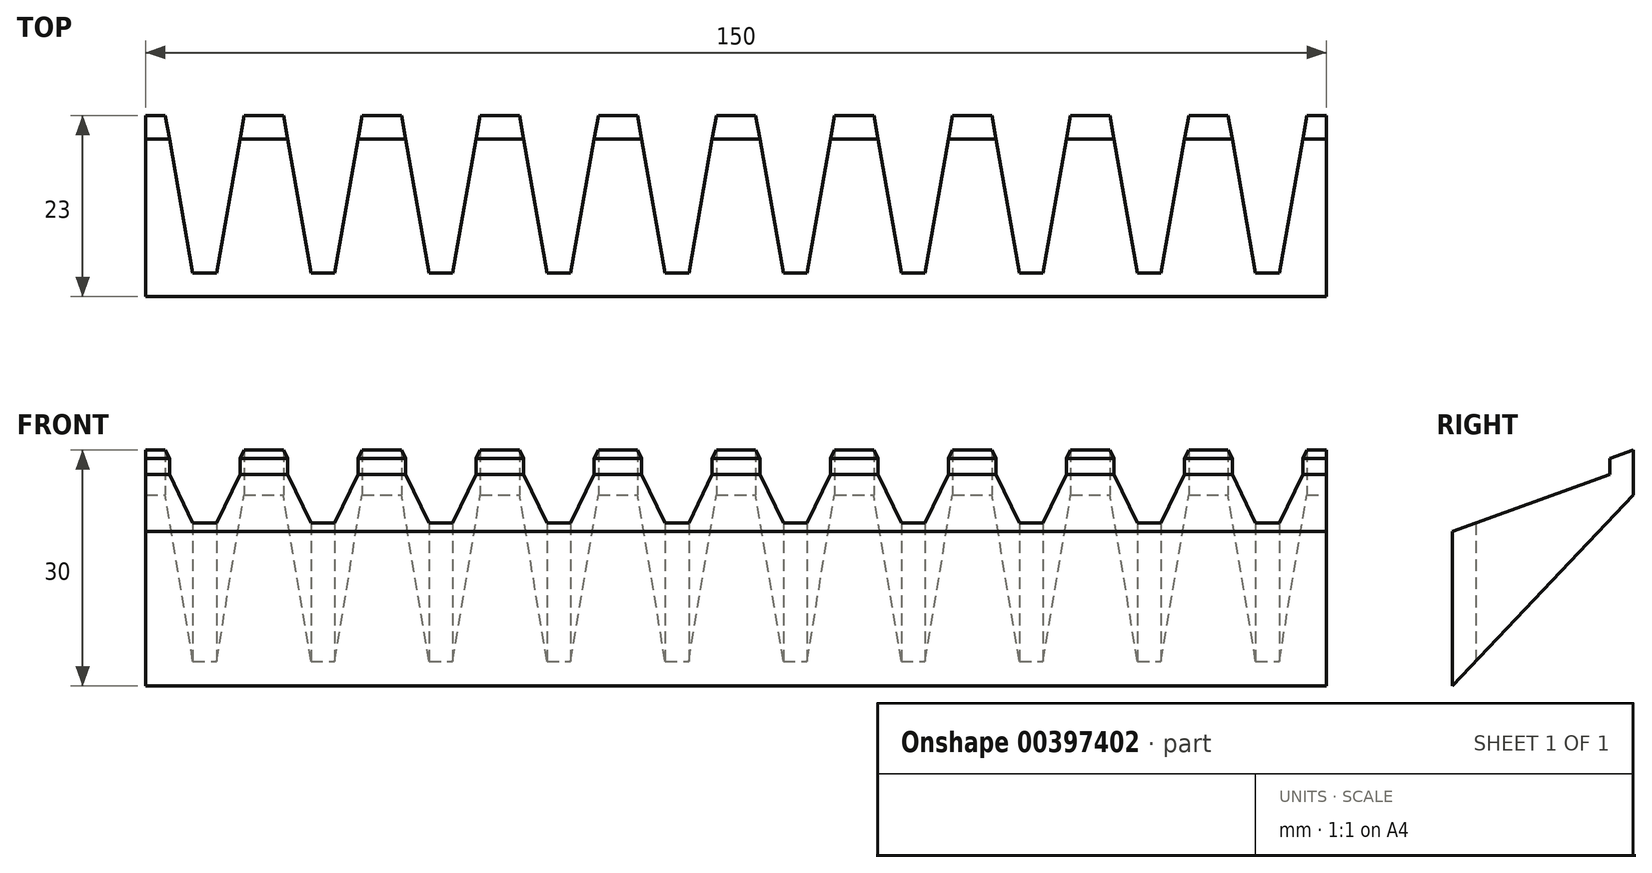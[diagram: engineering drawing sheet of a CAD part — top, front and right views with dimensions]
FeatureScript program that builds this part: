
annotation { "Feature Type Name" : "Feature", "Feature Type Description" : "" }
export const myFeature = defineFeature(function(context is Context, id is Id, definition is map)
    precondition{}
    {
        {
            var Q0;
            Q0=qCreatedBy(makeId("Top.planeOp"),FACE);
            var sketch = newSketch(context, id + "F0", { "sketchPlane" : qUnion([Q0])});
            skLineSegment(sketch, "E0", {"start": v(0, 0) * mm, "end": v(0, 52.8) * mm, "construction": true});
            skLineSegment(sketch, "E1", {"start": v(-7.5, 23) * mm, "end": v(-5, 23) * mm});
            skLineSegment(sketch, "E2", {"start": v(-5, 23) * mm, "end": v(-1.5, 3) * mm});
            skLineSegment(sketch, "E3", {"start": v(-1.5, 3) * mm, "end": v(0, 3) * mm});
            skLineSegment(sketch, "E4", {"start": v(-7.5, 23) * mm, "end": v(-7.5, 0) * mm});
            skLineSegment(sketch, "E5.MirrorCS", {"start": v(7.5, 23) * mm, "end": v(7.5, 0) * mm, "construction": true});
            skLineSegment(sketch, "E6.MirrorCS", {"start": v(5, 23) * mm, "end": v(1.5, 3) * mm});
            skLineSegment(sketch, "E7.MirrorCS", {"start": v(1.5, 3) * mm, "end": v(0, 3) * mm});
            skLineSegment(sketch, "E8.MirrorCS", {"start": v(7.5, 23) * mm, "end": v(5, 23) * mm});
            skLineSegment(sketch, "E9.1.0.0", {"start": v(20, 23) * mm, "end": v(16.5, 3) * mm});
            skLineSegment(sketch, "E9.1.0.1", {"start": v(22.5, 23) * mm, "end": v(20, 23) * mm});
            skLineSegment(sketch, "E9.1.0.2", {"start": v(22.5, 23) * mm, "end": v(22.5, 0) * mm, "construction": true});
            skLineSegment(sketch, "E9.1.0.4", {"start": v(10, 23) * mm, "end": v(13.5, 3) * mm});
            skLineSegment(sketch, "E9.1.0.5", {"start": v(7.5, 23) * mm, "end": v(10, 23) * mm});
            skLineSegment(sketch, "E9.1.0.6", {"start": v(16.5, 3) * mm, "end": v(15, 3) * mm});
            skLineSegment(sketch, "E9.1.0.7", {"start": v(13.5, 3) * mm, "end": v(15, 3) * mm});
            skLineSegment(sketch, "E9.2.0.0", {"start": v(35, 23) * mm, "end": v(31.5, 3) * mm});
            skLineSegment(sketch, "E9.2.0.1", {"start": v(37.5, 23) * mm, "end": v(35, 23) * mm});
            skLineSegment(sketch, "E9.2.0.2", {"start": v(37.5, 23) * mm, "end": v(37.5, 0) * mm, "construction": true});
            skLineSegment(sketch, "E9.2.0.3", {"start": v(22.5, 23) * mm, "end": v(22.5, 0) * mm, "construction": true});
            skLineSegment(sketch, "E9.2.0.4", {"start": v(25, 23) * mm, "end": v(28.5, 3) * mm});
            skLineSegment(sketch, "E9.2.0.5", {"start": v(22.5, 23) * mm, "end": v(25, 23) * mm});
            skLineSegment(sketch, "E9.2.0.6", {"start": v(31.5, 3) * mm, "end": v(30, 3) * mm});
            skLineSegment(sketch, "E9.2.0.7", {"start": v(28.5, 3) * mm, "end": v(30, 3) * mm});
            skLineSegment(sketch, "E9.3.0.0", {"start": v(50, 23) * mm, "end": v(46.5, 3) * mm});
            skLineSegment(sketch, "E9.3.0.1", {"start": v(52.5, 23) * mm, "end": v(50, 23) * mm});
            skLineSegment(sketch, "E9.3.0.2", {"start": v(52.5, 23) * mm, "end": v(52.5, 0) * mm, "construction": true});
            skLineSegment(sketch, "E9.3.0.3", {"start": v(37.5, 23) * mm, "end": v(37.5, 0) * mm, "construction": true});
            skLineSegment(sketch, "E9.3.0.4", {"start": v(40, 23) * mm, "end": v(43.5, 3) * mm});
            skLineSegment(sketch, "E9.3.0.5", {"start": v(37.5, 23) * mm, "end": v(40, 23) * mm});
            skLineSegment(sketch, "E9.3.0.6", {"start": v(46.5, 3) * mm, "end": v(45, 3) * mm});
            skLineSegment(sketch, "E9.3.0.7", {"start": v(43.5, 3) * mm, "end": v(45, 3) * mm});
            skLineSegment(sketch, "E9.4.0.0", {"start": v(65, 23) * mm, "end": v(61.5, 3) * mm});
            skLineSegment(sketch, "E9.4.0.1", {"start": v(67.5, 23) * mm, "end": v(65, 23) * mm});
            skLineSegment(sketch, "E9.4.0.2", {"start": v(67.5, 23) * mm, "end": v(67.5, 0) * mm, "construction": true});
            skLineSegment(sketch, "E9.4.0.3", {"start": v(52.5, 23) * mm, "end": v(52.5, 0) * mm, "construction": true});
            skLineSegment(sketch, "E9.4.0.4", {"start": v(55, 23) * mm, "end": v(58.5, 3) * mm});
            skLineSegment(sketch, "E9.4.0.5", {"start": v(52.5, 23) * mm, "end": v(55, 23) * mm});
            skLineSegment(sketch, "E9.4.0.6", {"start": v(61.5, 3) * mm, "end": v(60, 3) * mm});
            skLineSegment(sketch, "E9.4.0.7", {"start": v(58.5, 3) * mm, "end": v(60, 3) * mm});
            skLineSegment(sketch, "E9.5.0.0", {"start": v(80, 23) * mm, "end": v(76.5, 3) * mm});
            skLineSegment(sketch, "E9.5.0.1", {"start": v(82.5, 23) * mm, "end": v(80, 23) * mm});
            skLineSegment(sketch, "E9.5.0.2", {"start": v(82.5, 23) * mm, "end": v(82.5, 0) * mm, "construction": true});
            skLineSegment(sketch, "E9.5.0.3", {"start": v(67.5, 23) * mm, "end": v(67.5, 0) * mm, "construction": true});
            skLineSegment(sketch, "E9.5.0.4", {"start": v(70, 23) * mm, "end": v(73.5, 3) * mm});
            skLineSegment(sketch, "E9.5.0.5", {"start": v(67.5, 23) * mm, "end": v(70, 23) * mm});
            skLineSegment(sketch, "E9.5.0.6", {"start": v(76.5, 3) * mm, "end": v(75, 3) * mm});
            skLineSegment(sketch, "E9.5.0.7", {"start": v(73.5, 3) * mm, "end": v(75, 3) * mm});
            skLineSegment(sketch, "E9.6.0.0", {"start": v(95, 23) * mm, "end": v(91.5, 3) * mm});
            skLineSegment(sketch, "E9.6.0.1", {"start": v(97.5, 23) * mm, "end": v(95, 23) * mm});
            skLineSegment(sketch, "E9.6.0.2", {"start": v(97.5, 23) * mm, "end": v(97.5, 0) * mm, "construction": true});
            skLineSegment(sketch, "E9.6.0.3", {"start": v(82.5, 23) * mm, "end": v(82.5, 0) * mm, "construction": true});
            skLineSegment(sketch, "E9.6.0.4", {"start": v(85, 23) * mm, "end": v(88.5, 3) * mm});
            skLineSegment(sketch, "E9.6.0.5", {"start": v(82.5, 23) * mm, "end": v(85, 23) * mm});
            skLineSegment(sketch, "E9.6.0.6", {"start": v(91.5, 3) * mm, "end": v(90, 3) * mm});
            skLineSegment(sketch, "E9.6.0.7", {"start": v(88.5, 3) * mm, "end": v(90, 3) * mm});
            skLineSegment(sketch, "E9.7.0.0", {"start": v(110, 23) * mm, "end": v(106.5, 3) * mm});
            skLineSegment(sketch, "E9.7.0.1", {"start": v(112.5, 23) * mm, "end": v(110, 23) * mm});
            skLineSegment(sketch, "E9.7.0.2", {"start": v(112.5, 23) * mm, "end": v(112.5, 0) * mm, "construction": true});
            skLineSegment(sketch, "E9.7.0.3", {"start": v(97.5, 23) * mm, "end": v(97.5, 0) * mm, "construction": true});
            skLineSegment(sketch, "E9.7.0.4", {"start": v(100, 23) * mm, "end": v(103.5, 3) * mm});
            skLineSegment(sketch, "E9.7.0.5", {"start": v(97.5, 23) * mm, "end": v(100, 23) * mm});
            skLineSegment(sketch, "E9.7.0.6", {"start": v(106.5, 3) * mm, "end": v(105, 3) * mm});
            skLineSegment(sketch, "E9.7.0.7", {"start": v(103.5, 3) * mm, "end": v(105, 3) * mm});
            skLineSegment(sketch, "E9.8.0.0", {"start": v(125, 23) * mm, "end": v(121.5, 3) * mm});
            skLineSegment(sketch, "E9.8.0.1", {"start": v(127.5, 23) * mm, "end": v(125, 23) * mm});
            skLineSegment(sketch, "E9.8.0.2", {"start": v(127.5, 23) * mm, "end": v(127.5, 0) * mm, "construction": true});
            skLineSegment(sketch, "E9.8.0.3", {"start": v(112.5, 23) * mm, "end": v(112.5, 0) * mm, "construction": true});
            skLineSegment(sketch, "E9.8.0.4", {"start": v(115, 23) * mm, "end": v(118.5, 3) * mm});
            skLineSegment(sketch, "E9.8.0.5", {"start": v(112.5, 23) * mm, "end": v(115, 23) * mm});
            skLineSegment(sketch, "E9.8.0.6", {"start": v(121.5, 3) * mm, "end": v(120, 3) * mm});
            skLineSegment(sketch, "E9.8.0.7", {"start": v(118.5, 3) * mm, "end": v(120, 3) * mm});
            skLineSegment(sketch, "E9.9.0.0", {"start": v(140, 23) * mm, "end": v(136.5, 3) * mm});
            skLineSegment(sketch, "E9.9.0.1", {"start": v(142.5, 23) * mm, "end": v(140, 23) * mm});
            skLineSegment(sketch, "E9.9.0.2", {"start": v(142.5, 23) * mm, "end": v(142.5, 0) * mm});
            skLineSegment(sketch, "E9.9.0.3", {"start": v(127.5, 23) * mm, "end": v(127.5, 0) * mm, "construction": true});
            skLineSegment(sketch, "E9.9.0.4", {"start": v(130, 23) * mm, "end": v(133.5, 3) * mm});
            skLineSegment(sketch, "E9.9.0.5", {"start": v(127.5, 23) * mm, "end": v(130, 23) * mm});
            skLineSegment(sketch, "E9.9.0.6", {"start": v(136.5, 3) * mm, "end": v(135, 3) * mm});
            skLineSegment(sketch, "E9.9.0.7", {"start": v(133.5, 3) * mm, "end": v(135, 3) * mm});
            skLineSegment(sketch, "E9.direction1", {"start": v(-7.5, 0) * mm, "end": v(7.5, 0) * mm, "construction": true});
            skLineSegment(sketch, "E10", {"start": v(-7.5, 0) * mm, "end": v(142.5, 0) * mm});
            skSolve(sketch);
        }
        {
            var Q0;
            Q0 = qSketchRegion(id + "F0", true);
            extrude(context, id + "F1", {"entities" : qUnion([Q0]), "depth" : 30 * mm});
        }
        {
            var Q0;
            Q0=makeQuery(id+"F1.opExtrude","SWEPT_FACE",FACE,{"disambiguationData":[OSD([sQuery(id+"F0.wireOp",EDGE,"E9.9.0.2")])]});
            var sketch = newSketch(context, id + "F2", { "sketchPlane" : qUnion([Q0])});
            skLineSegment(sketch, "E11", {"start": v(23, 30) * mm, "end": v(20, 28.9) * mm});
            skLineSegment(sketch, "E12", {"start": v(20, 28.9) * mm, "end": v(20, 26.9) * mm});
            skLineSegment(sketch, "E13", {"start": v(20, 26.9) * mm, "end": v(0, 19.63) * mm});
            skLineSegment(sketch, "E14", {"start": v(0, 19.63) * mm, "end": v(0, 30) * mm});
            skLineSegment(sketch, "E15", {"start": v(0, 30) * mm, "end": v(23, 30) * mm});
            skLineSegment(sketch, "E16", {"start": v(0, 0) * mm, "end": v(23, 24.26) * mm});
            skLineSegment(sketch, "E17", {"start": v(23, 24.26) * mm, "end": v(23, 0) * mm});
            skLineSegment(sketch, "E18", {"start": v(23, 0) * mm, "end": v(0, 0) * mm});
            skSolve(sketch);
        }
        {
            var Q0;
            Q0 = qSketchRegion(id + "F2", true);
            extrude(context, id + "F3", {"entities" : qUnion([Q0]), "operationType" : NewBodyOperationType.REMOVE, "endBound" : BoundingType.THROUGH_ALL, "oppositeDirection" : true, "depth" : 25 * mm});
        }
    });
